# Revit family: 2014_Ventana_Balconera-Practicable-1-Hoja-Monoblock_Alugom_Serie-ALG-75-Máxima
name_source: partatom
category: Ventanas
revit_build: Autodesk Revit 2014 (Build: 20130308_1515(x64)
units: mm (PartAtom-declared; Revit-internal decimal feet)

## types (1)
- Ventana 1 Hoja Balconera con Monoblock 1230x2200 mm
    * Info = Ventana de 2 hojas de 1230x1480 mm
    ** Info = Ventana de 1 hoja de 1230x1480 mm; Vidrio Uv: 0,7W(m²K)
    *** Info = Ventana de 2 hojas de 1230x1480 mm; Vidrio Rw: 40 (-2,-6) dB
    ACCESORIOS_1306-Escuadra exterior = 8
    ACCESORIOS_4008-Patín apoyo hoja = 1
    ACCESORIOS_4337-Embellecedor salida agua = 2
    ACCESORIOS_4390-Bisagra pract. = 2
    ACCESORIOS_4613-Mecanismo cuadradillo pract. = 1
    ACCESORIOS_4710-Escuadra alineamiento (14mm) = 12
    ACCESORIOS_4720-Cerradero lateral doble = 2
    ACCESORIOS_4739-Terminal pletina metálico = 2
    ACCESORIOS_4850-Junta exterior acrist. c/alas (H) = 2
    ACCESORIOS_4850-Junta exterior acrist. c/alas (L) = 2
    ACCESORIOS_5073-Junta central alg (H) = 2
    ACCESORIOS_5073-Junta central alg (L) = 2
    ACCESORIOS_5074-Refuerzo junta central (H) = 2
    ACCESORIOS_5074-Refuerzo junta central (L) = 2
    ACCESORIOS_5079-Manilla Inox recta = 1
    ACCESORIOS_5085 Junta perimetral hoja alg (H) = 2
    ACCESORIOS_5085 Junta perimetral hoja alg (L) = 2
    ACCESORIOS_5104-Escuadra balconera = 8
    ACCESORIOS_5105-Ángulo vulcanizado junta central = 4
    Acristalamiento = Vidrio
    Aislamiento acústico*** = 44 (-1,-5) dB
    Altura = 2385 mm  [stored 7.8248 ft]
    Altura Cristal = 2074 mm  [stored 6.80446 ft]
    Altura Hoja = 2358 mm  [stored 7.73622 ft]
    Altura Real = 2385 mm  [stored 7.8248 ft]
    Altura Ventana = 2200 mm  [stored 7.21785 ft]
    Altura Ventana Real = 2200 mm  [stored 7.21785 ft]
    Altura de antepecho por defecto = 0 mm  [stored 0 ft]
    Anchura = 1339.4 mm  [stored 4.39436 ft]
    Anchura Real = 1339.4 mm  [stored 4.39436 ft]
    Anchura Ventana = 1230 mm  [stored 4.03543 ft]
    Anchura Ventana Real = 1230 mm  [stored 4.03543 ft]
    Bimetica = http://www.bimetica.com
    Cierre de muro = Por anfitrión
    Comentarios de tipo = UNA VENTANA TOP CON LA EFICIENCIA ENERGETICA DEL FUTURO
Con la nueva ALG 75 MAXIMA y su valor medio Uf de 1,26 W/m2K el ahorro en calefacción está asegurado. Este sistema de carpintería posee una eficiencia energética mayor que muchas ventanas de PVC o madera, satisfaciendo los requisitos mas exigentes en aislamiento térmico. Y todo ello, sin renunciar a las ventajas de resistencia, durabilidad, elegancia y posibilidades de diseño del aluminio. Estos increíbles valores de aislamiento térmico se consiguen mediante las poliamidas de 'alas' y 'celdas', la doble junta central y la colocación de 'foam' por debajo del cristal.
Se trata de un sistema de carpintería de tres cámaras con rotura de puente térmico para puertas y ventanas, que con un diseño robusto, una gran versatilidad  y un alto aislamiento térmico, está especialmente diseñado para que el montaje sea fácil. La hoja de 81 mm de esta ventana permite hasta 60 mm de galce, pudiéndose realizar grandes ventanales para mejorar el confort y la luminosidad de las viviendas o edificios. 

Ventana de elegante sofisticación ideal para quien busque una arquitectura sostenible con un diseño vanguardista.
    Configuración de Poliamidas = Poliamidas P66 GF25Technoform Bautec de la serie Standar. Referencias: 429300, 268400, 425100, 380000, 951459
    Creado por = Bimetica Parametric Design Services S.L.
    Descripción = Ventana 1 hoja balconera con rotura de puente térmico y Monoblock
    Estanqueidad al aire* = CLASE E1650
    Fabricante = Grupo ALUGOM
    Fecha Revisión de Contenido = 26/10/2015
    Fecha de Caducidad de la Información = 01/01/2016
    Grosor Acristalamiento = 39 mm  [stored 0.127953 ft]
    Grosor Acristalamiento Control = 39 mm  [stored 0.127953 ft]
    Línea Proyección = 1151.5 mm  [stored 3.77789 ft]
    Marco = Aluminio
    Masterformat Código = 08 51 13
    Masterformat Descripción = Aluminium Windows
    Modelo = Serie ALG 75 MAXIMA
    Omniclass Código = 23.30.20.17.21.21
    Omniclass Título = Casment Window
    PERFILES_16-H-Cerco balconera alg 75_Horizontal = 2
    PERFILES_16-H-Cerco balconera alg 75_Vertical = 2
    PERFILES_16-H-Hoja balconera alg 75_Horizontal = 2
    PERFILES_16-H-Hoja balconera alg 75_Vertical = 2
    PERFILES_8412-Pletina falleba_Vertical = 0
    PERFILES_8428-Vierteaguas_Horizontal = 1
    PERFILES_Junquillo 22mm_Horizontal = 2
    PERFILES_Junquillo 22mm_Vertical = 2
    Permeabilidad al aire* = CLASE 4
    Poliamida = Poliamida, Technoform Bautec, PA66 GF 25
    Resistencia al viento* = CLASE C5
    Sección de Hoja = 82 mm  [stored 0.269029 ft]
    Sección de Marco = 75 mm
    Transmitancia térmica** = 1.3 W(m²K)
    UNSPSC Categoría = 30171600
    UNSPSC Código = Windows
    URL = http://www.alugom.com
    URL Poliamida = http://www.technoform.es
    URL Poliamida - Catálogo = http://www.technoform.com
    URL Producto = http://www.alugom.com
    Uniclass 2.0 Código = 25-30
    Uniclass 2.0 Descripción = Door and window systems

note: [stored X ft] marks values corroborated as IEEE doubles in the binary element streams (Revit-internal decimal feet)

## geometry (parser evidence)
native form markers: Blend x4
no freeform markers — native parametric forms only
